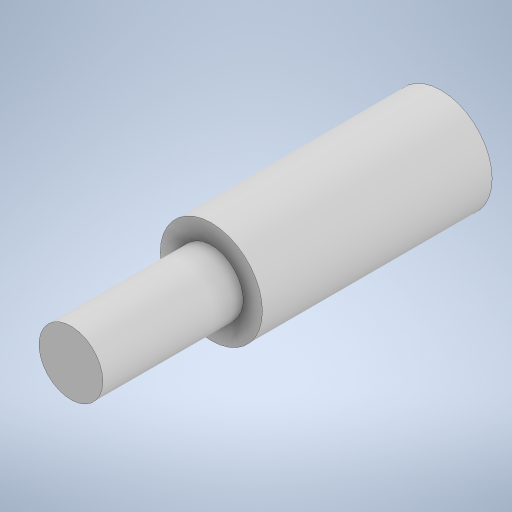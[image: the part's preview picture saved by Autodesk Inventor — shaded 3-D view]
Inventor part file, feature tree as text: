
AUTODESK INVENTOR PART (.ipt)
format: ipt  version: 2023.5 (Build 275446000, 446)  size: 237,056 bytes
history: native  units: in
note: dims shown in document units (in); Inventor stores cm internally (conversion verified against a paired STEP export)
features: extrude x3, sketch x3
ambient origin geometry x8: Origin, YZ Plane, XZ Plane, XY Plane, X Axis, Y Axis, Z Axis, Center Point
bodies: Solid1 (feature_tree)
feature tree (6):
  extrude  "Extrusion1"  Depth=0.5709in TaperAngle=0.0deg
  extrude  "Extrusion3"  Depth=0.3543in TaperAngle=0.0deg
  extrude  "Extrusion4"  [1 undecoded]
  sketch  "Sketch1"  dims[d0=0.0984in d1=0.5709in d2=0.0in]
  sketch  "Sketch3"  dims[d6=0.1575in d7=0.3543in d8=0.0in]
  sketch  "Sketch4"  dims[d9=0.1969in d10=0.0in]
note: 1 required parameter value undecoded (feature->parameter linkage not recoverable at this tier; creation-order binding heuristic only, values carry confidence <= 0.55)
